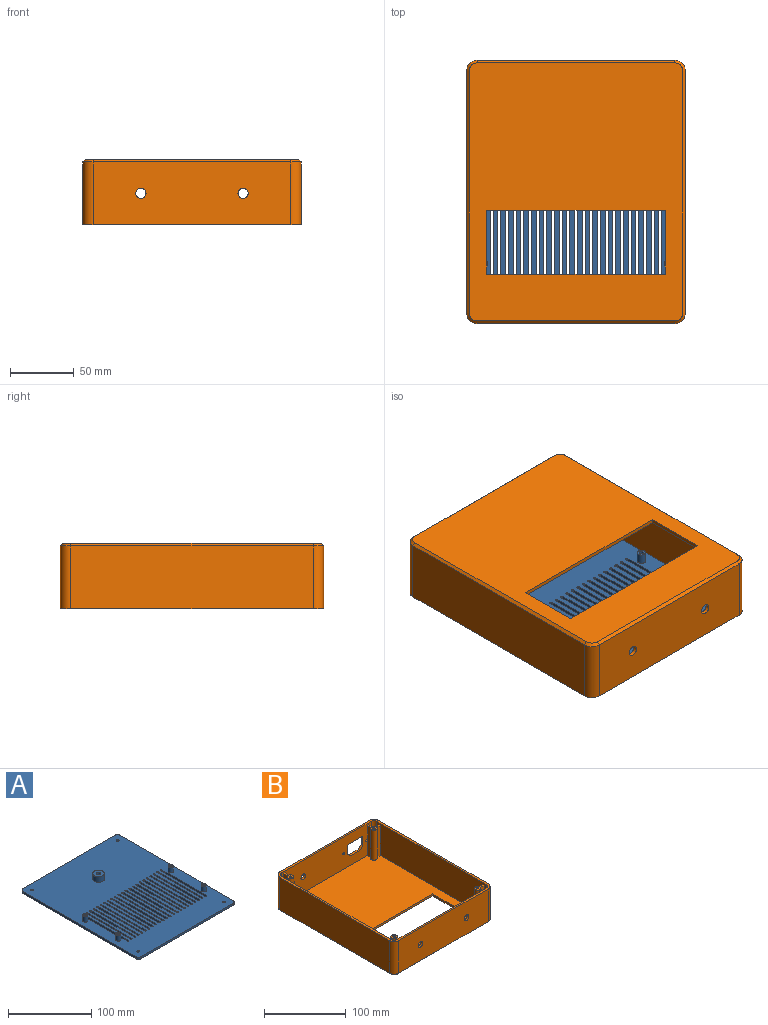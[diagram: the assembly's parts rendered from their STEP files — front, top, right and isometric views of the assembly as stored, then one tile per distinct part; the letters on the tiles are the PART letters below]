
ASSEMBLY  parts=2 mates=1
PART A: 126 faces, bbox 165x200x11 mm
  f0: plane 200x165mm, normal (0,0,1), area 28777.3mm2, adj f2,f3,f4,f5,f6,f9,f12,f15
  f1: plane 200x165mm, normal (0,0,-1), area 29063.9mm2, adj f2,f3,f4,f5,f21,f22,f23,f24
  f2: plane 155x3mm, normal (0,-1,0), area 465mm2, adj f0,f1,f21,f24
  f3: plane 190x3mm, normal (1,0,0), area 570mm2, adj f0,f1,f21,f22
  f4: plane 155x3mm, normal (0,1,0), area 465mm2, adj f0,f1,f22,f23
  f5: plane 190x3mm, normal (-1,0,0), area 570mm2, adj f0,f1,f23,f24
  f6: cylinder r=3.25mm len=8mm, axis (0,0,-1), area 163.4mm2, adj f0,f7
  f7: plane 6.5x6.5mm, normal (0,0,1), area 25.6mm2, adj f6,f28
  f8: plane 2.9x2.9mm, normal (0,0,1), area 6.6mm2, adj f28
  f9: cylinder r=3.25mm len=8mm, axis (0,0,-1), area 163.4mm2, adj f0,f10
  f10: plane 6.5x6.5mm, normal (0,0,1), area 25.6mm2, adj f9,f29
  f11: plane 2.9x2.9mm, normal (0,0,1), area 6.6mm2, adj f29
  f12: cylinder r=3.25mm len=8mm, axis (0,0,-1), area 163.4mm2, adj f0,f13
  f13: plane 6.5x6.5mm, normal (0,0,1), area 25.6mm2, adj f12,f26
  f14: plane 2.9x2.9mm, normal (0,0,1), area 6.6mm2, adj f26
  f15: cylinder r=3.25mm len=8mm, axis (0,0,-1), area 163.4mm2, adj f0,f16
  f16: plane 6.5x6.5mm, normal (0,0,1), area 25.6mm2, adj f15,f27
  f17: plane 2.9x2.9mm, normal (0,0,1), area 6.6mm2, adj f27
  f18: cylinder r=7mm len=14mm, axis (0,0,-1), area 351.9mm2, adj f0,f19
  f19: plane 14x14mm, normal (0,0,1), area 132.7mm2, adj f18,f25
  f20: plane 4.8x4.8mm, normal (0,0,1), area 18.1mm2, adj f25
  f21: cylinder r=5mm len=5mm, axis (0,0,1), area 23.6mm2, adj f0,f1,f2,f3
  f22: cylinder r=5mm len=5mm, axis (0,0,-1), area 23.6mm2, adj f0,f1,f3,f4
  f23: cylinder r=5mm len=5mm, axis (0,0,1), area 23.6mm2, adj f0,f1,f4,f5
  f24: cylinder r=5mm len=5mm, axis (0,0,-1), area 23.6mm2, adj f0,f1,f2,f5
  f25: cone r=2.4mm half-angle=1.4deg, axis (0,0,1), area 125.7mm2, adj f19,f20
  f26: cone r=1.45mm half-angle=0.7deg, axis (0,0,1), area 75.4mm2, adj f13,f14
  f27: cone r=1.45mm half-angle=0.7deg, axis (0,0,1), area 75.4mm2, adj f16,f17
  f28: cone r=1.45mm half-angle=0.7deg, axis (0,0,1), area 75.4mm2, adj f7,f8
  f29: cone r=1.45mm half-angle=0.7deg, axis (0,0,1), area 75.4mm2, adj f10,f11
  f30: cylinder r=1.1mm len=3mm, axis (0,0,1), area 10.4mm2, adj f0,f1,f31,f32
  f31: plane 75x3mm, normal (-1,0,0), area 225mm2, adj f0,f1,f30,f33
  f32: plane 75x3mm, normal (1,0,0), area 225mm2, adj f0,f1,f30,f33
  f33: cylinder r=1.1mm len=3mm, axis (0,0,1), area 10.4mm2, adj f0,f1,f31,f32
  f34: plane 75x3mm, normal (1,0,0), area 225mm2, adj f0,f1,f35,f36
  f35: cylinder r=1.1mm len=3mm, axis (0,0,1), area 10.4mm2, adj f0,f1,f34,f37
  f36: cylinder r=1.1mm len=3mm, axis (0,0,1), area 10.4mm2, adj f0,f1,f34,f37
  f37: plane 75x3mm, normal (-1,0,0), area 225mm2, adj f0,f1,f35,f36
  f38: plane 75x3mm, normal (-1,0,0), area 225mm2, adj f0,f1,f39,f41
  f39: cylinder r=1.1mm len=3mm, axis (0,0,1), area 10.4mm2, adj f0,f1,f38,f40
  f40: plane 75x3mm, normal (1,0,0), area 225mm2, adj f0,f1,f39,f41
  f41: cylinder r=1.1mm len=3mm, axis (0,0,1), area 10.4mm2, adj f0,f1,f38,f40
  f42: plane 75x3mm, normal (1,0,0), area 225mm2, adj f0,f1,f43,f44
  f43: cylinder r=1.1mm len=3mm, axis (0,0,1), area 10.4mm2, adj f0,f1,f42,f45
  f44: cylinder r=1.1mm len=3mm, axis (0,0,1), area 10.4mm2, adj f0,f1,f42,f45
  f45: plane 75x3mm, normal (-1,0,0), area 225mm2, adj f0,f1,f43,f44
  f46: plane 75x3mm, normal (-1,0,0), area 225mm2, adj f0,f1,f47,f49
  f47: cylinder r=1.1mm len=3mm, axis (0,0,1), area 10.4mm2, adj f0,f1,f46,f48
  f48: plane 75x3mm, normal (1,0,0), area 225mm2, adj f0,f1,f47,f49
  f49: cylinder r=1.1mm len=3mm, axis (0,0,1), area 10.4mm2, adj f0,f1,f46,f48
  f50: plane 75x3mm, normal (-1,0,0), area 225mm2, adj f0,f1,f51,f53
  f51: cylinder r=1.1mm len=3mm, axis (0,0,1), area 10.4mm2, adj f0,f1,f50,f52
  f52: plane 75x3mm, normal (1,0,0), area 225mm2, adj f0,f1,f51,f53
  f53: cylinder r=1.1mm len=3mm, axis (0,0,1), area 10.4mm2, adj f0,f1,f50,f52
  f54: plane 75x3mm, normal (-1,0,0), area 225mm2, adj f0,f1,f55,f57
  f55: cylinder r=1.1mm len=3mm, axis (0,0,1), area 10.4mm2, adj f0,f1,f54,f56
  f56: plane 75x3mm, normal (1,0,0), area 225mm2, adj f0,f1,f55,f57
  f57: cylinder r=1.1mm len=3mm, axis (0,0,1), area 10.4mm2, adj f0,f1,f54,f56
  f58: cylinder r=1.1mm len=3mm, axis (0,0,1), area 10.4mm2, adj f0,f1,f59,f61
  f59: plane 75x3mm, normal (-1,0,0), area 225mm2, adj f0,f1,f58,f60
  f60: cylinder r=1.1mm len=3mm, axis (0,0,1), area 10.4mm2, adj f0,f1,f59,f61
  f61: plane 75x3mm, normal (1,0,0), area 225mm2, adj f0,f1,f58,f60
  f62: cylinder r=1.1mm len=3mm, axis (0,0,1), area 10.4mm2, adj f0,f1,f63,f65
  f63: plane 75x3mm, normal (-1,0,0), area 225mm2, adj f0,f1,f62,f64
  f64: cylinder r=1.1mm len=3mm, axis (0,0,1), area 10.4mm2, adj f0,f1,f63,f65
  f65: plane 75x3mm, normal (1,0,0), area 225mm2, adj f0,f1,f62,f64
  f66: cylinder r=1.1mm len=3mm, axis (0,0,1), area 10.4mm2, adj f0,f1,f67,f69
  f67: plane 75x3mm, normal (-1,0,0), area 225mm2, adj f0,f1,f66,f68
  f68: cylinder r=1.1mm len=3mm, axis (0,0,1), area 10.4mm2, adj f0,f1,f67,f69
  f69: plane 75x3mm, normal (1,0,0), area 225mm2, adj f0,f1,f66,f68
  f70: cylinder r=1.1mm len=3mm, axis (0,0,1), area 10.4mm2, adj f0,f1,f71,f73
  f71: plane 75x3mm, normal (-1,0,0), area 225mm2, adj f0,f1,f70,f72
  f72: cylinder r=1.1mm len=3mm, axis (0,0,1), area 10.4mm2, adj f0,f1,f71,f73
  f73: plane 75x3mm, normal (1,0,0), area 225mm2, adj f0,f1,f70,f72
  f74: cylinder r=1.1mm len=3mm, axis (0,0,1), area 10.4mm2, adj f0,f1,f75,f77
  f75: plane 75x3mm, normal (-1,0,0), area 225mm2, adj f0,f1,f74,f76
  f76: cylinder r=1.1mm len=3mm, axis (0,0,1), area 10.4mm2, adj f0,f1,f75,f77
  f77: plane 75x3mm, normal (1,0,0), area 225mm2, adj f0,f1,f74,f76
  f78: cylinder r=1.1mm len=3mm, axis (0,0,1), area 10.4mm2, adj f0,f1,f79,f81
  f79: plane 75x3mm, normal (-1,0,0), area 225mm2, adj f0,f1,f78,f80
  f80: cylinder r=1.1mm len=3mm, axis (0,0,1), area 10.4mm2, adj f0,f1,f79,f81
  f81: plane 75x3mm, normal (1,0,0), area 225mm2, adj f0,f1,f78,f80
  f82: cylinder r=1.1mm len=3mm, axis (0,0,1), area 10.4mm2, adj f0,f1,f83,f85
  f83: plane 75x3mm, normal (-1,0,0), area 225mm2, adj f0,f1,f82,f84
  f84: cylinder r=1.1mm len=3mm, axis (0,0,1), area 10.4mm2, adj f0,f1,f83,f85
  f85: plane 75x3mm, normal (1,0,0), area 225mm2, adj f0,f1,f82,f84
  f86: cylinder r=1.1mm len=3mm, axis (0,0,1), area 10.4mm2, adj f0,f1,f87,f89
  f87: plane 75x3mm, normal (-1,0,0), area 225mm2, adj f0,f1,f86,f88
  f88: cylinder r=1.1mm len=3mm, axis (0,0,1), area 10.4mm2, adj f0,f1,f87,f89
  f89: plane 75x3mm, normal (1,0,0), area 225mm2, adj f0,f1,f86,f88
  f90: plane 75x3mm, normal (-1,0,0), area 225mm2, adj f0,f1,f91,f93
  f91: cylinder r=1.1mm len=3mm, axis (0,0,1), area 10.4mm2, adj f0,f1,f90,f92
  f92: plane 75x3mm, normal (1,0,0), area 225mm2, adj f0,f1,f91,f93
  f93: cylinder r=1.1mm len=3mm, axis (0,0,1), area 10.4mm2, adj f0,f1,f90,f92
  f94: cylinder r=1.1mm len=3mm, axis (0,0,1), area 10.4mm2, adj f0,f1,f95,f97
  f95: plane 75x3mm, normal (-1,0,0), area 225mm2, adj f0,f1,f94,f96
  f96: cylinder r=1.1mm len=3mm, axis (0,0,1), area 10.4mm2, adj f0,f1,f95,f97
  f97: plane 75x3mm, normal (1,0,0), area 225mm2, adj f0,f1,f94,f96
  f98: cylinder r=1.1mm len=3mm, axis (0,0,1), area 10.4mm2, adj f0,f1,f99,f101
  f99: plane 75x3mm, normal (-1,0,0), area 225mm2, adj f0,f1,f98,f100
  f100: cylinder r=1.1mm len=3mm, axis (0,0,1), area 10.4mm2, adj f0,f1,f99,f101
  f101: plane 75x3mm, normal (1,0,0), area 225mm2, adj f0,f1,f98,f100
  f102: cylinder r=1.1mm len=3mm, axis (0,0,1), area 10.4mm2, adj f0,f1,f103,f105
  f103: plane 75x3mm, normal (-1,0,0), area 225mm2, adj f0,f1,f102,f104
  f104: cylinder r=1.1mm len=3mm, axis (0,0,1), area 10.4mm2, adj f0,f1,f103,f105
  f105: plane 75x3mm, normal (1,0,0), area 225mm2, adj f0,f1,f102,f104
  f106: plane 75x3mm, normal (-1,0,0), area 225mm2, adj f0,f1,f107,f109
  f107: cylinder r=1.1mm len=3mm, axis (0,0,1), area 10.4mm2, adj f0,f1,f106,f108
  f108: plane 75x3mm, normal (1,0,0), area 225mm2, adj f0,f1,f107,f109
  f109: cylinder r=1.1mm len=3mm, axis (0,0,1), area 10.4mm2, adj f0,f1,f106,f108
  f110: plane 75x3mm, normal (-1,0,0), area 225mm2, adj f0,f1,f111,f113
  f111: cylinder r=1.1mm len=3mm, axis (0,0,1), area 10.4mm2, adj f0,f1,f110,f112
  f112: plane 75x3mm, normal (1,0,0), area 225mm2, adj f0,f1,f111,f113
  f113: cylinder r=1.1mm len=3mm, axis (0,0,1), area 10.4mm2, adj f0,f1,f110,f112
  f114: plane 75x3mm, normal (-1,0,0), area 225mm2, adj f0,f1,f115,f117
  f115: cylinder r=1.1mm len=3mm, axis (0,0,1), area 10.4mm2, adj f0,f1,f114,f116
  f116: plane 75x3mm, normal (1,0,0), area 225mm2, adj f0,f1,f115,f117
  f117: cylinder r=1.1mm len=3mm, axis (0,0,1), area 10.4mm2, adj f0,f1,f114,f116
  f118: plane 75x3mm, normal (1,0,0), area 225mm2, adj f0,f1,f119,f120
  f119: cylinder r=1.1mm len=3mm, axis (0,0,1), area 10.4mm2, adj f0,f1,f118,f121
  f120: cylinder r=1.1mm len=3mm, axis (0,0,1), area 10.4mm2, adj f0,f1,f118,f121
  f121: plane 75x3mm, normal (-1,0,0), area 225mm2, adj f0,f1,f119,f120
  f122: cylinder r=1.6mm len=3.2mm, axis (0,0,1), area 30.2mm2, adj f0,f1
  f123: cylinder r=1.6mm len=3.2mm, axis (0,0,1), area 30.2mm2, adj f0,f1
  f124: cylinder r=1.6mm len=3.2mm, axis (0,0,1), area 30.2mm2, adj f0,f1
  f125: cylinder r=1.6mm len=3.2mm, axis (0,0,1), area 30.2mm2, adj f0,f1
PART B: 84 faces, bbox 171x206x51 mm
  f0: plane 8.9x8.9mm, normal (0,0,1), area 68.8mm2, adj f2,f3,f8,f26,f76,f82
  f1: plane 200x165mm, normal (0,0,1), area 25396mm2, adj f2,f6,f7,f8,f10,f14,f33,f37
  f2: plane 155x48mm, normal (0,-1,0), area 6643.1mm2, adj f0,f1,f4,f15,f25,f26,f36,f40
  f3: cylinder r=4mm len=45mm, axis (0,0,-1), area 182.5mm2, adj f0,f36,f76,f82
  f4: plane 8.9x8.9mm, normal (0,0,1), area 68.8mm2, adj f2,f5,f6,f25,f77,f81
  f5: cylinder r=4mm len=45mm, axis (0,0,-1), area 182.5mm2, adj f4,f40,f77,f81
  f6: plane 190x48mm, normal (-1,0,0), area 8922mm2, adj f1,f4,f9,f15,f25,f28,f32,f40
  f7: cylinder r=4mm len=45mm, axis (0,0,-1), area 747.9mm2, adj f1,f40,f78,f80
  f8: plane 190x48mm, normal (1,0,0), area 8922mm2, adj f0,f1,f13,f15,f26,f27,f29,f36
  f9: plane 8.9x8.9mm, normal (0,0,1), area 68.8mm2, adj f6,f10,f11,f28,f72,f74
  f10: plane 155x48mm, normal (0,1,0), area 7141.5mm2, adj f1,f9,f13,f15,f27,f28,f29,f32
  f11: cylinder r=4mm len=45mm, axis (0,0,-1), area 182.5mm2, adj f9,f32,f72,f74
  f12: cylinder r=4mm len=45mm, axis (0,0,-1), area 182.5mm2, adj f13,f29,f67,f69
  f13: plane 8.9x8.9mm, normal (0,0,1), area 68.8mm2, adj f8,f10,f12,f27,f67,f69
  f14: cylinder r=4mm len=45mm, axis (0,0,-1), area 747.9mm2, adj f1,f29,f68,f70
  f15: plane 206x171mm, normal (0,0,1), area 2192.5mm2, adj f2,f6,f8,f10,f16,f17,f18,f19
  f16: plane 190x49mm, normal (1,0,0), area 9310mm2, adj f15,f21,f24,f43
  f17: plane 155x49mm, normal (0,1,0), area 6996mm2, adj f15,f21,f22,f46,f53,f54,f55,f56
  f18: plane 190x49mm, normal (-1,0,0), area 9310mm2, adj f15,f22,f23,f50
  f19: plane 155x49mm, normal (0,-1,0), area 7494.5mm2, adj f15,f23,f24,f47,f51,f52
  f20: plane 202x167mm, normal (0,0,-1), area 26703.1mm2, adj f43,f44,f45,f46,f47,f48,f49,f50
  f21: cylinder r=8mm len=49mm, axis (0,0,1), area 615.8mm2, adj f15,f16,f17,f44
  f22: cylinder r=8mm len=49mm, axis (0,0,-1), area 615.8mm2, adj f15,f17,f18,f48
  f23: cylinder r=8mm len=49mm, axis (0,0,1), area 615.8mm2, adj f15,f18,f19,f49
  f24: cylinder r=8mm len=49mm, axis (0,0,-1), area 615.8mm2, adj f15,f16,f19,f45
  f25: cylinder r=5mm len=48mm, axis (0,0,1), area 377mm2, adj f2,f4,f6,f15
  f26: cylinder r=5mm len=48mm, axis (0,0,-1), area 377mm2, adj f0,f2,f8,f15
  f27: cylinder r=5mm len=48mm, axis (0,0,1), area 377mm2, adj f8,f10,f13,f15
  f28: cylinder r=5mm len=48mm, axis (0,0,-1), area 377mm2, adj f6,f9,f10,f15
  f29: plane 14x14mm, normal (0,0,1), area 70.3mm2, adj f8,f10,f12,f14,f30,f67,f68,f69
  f30: cylinder r=1.45mm len=45mm, axis (0,0,-1), area 410mm2, adj f29,f31
  f31: plane 2.9x2.9mm, normal (0,0,1), area 6.6mm2, adj f30
  f32: plane 14x14mm, normal (0,0,1), area 70.3mm2, adj f6,f10,f11,f33,f34,f71,f72,f73
  f33: cylinder r=4mm len=45mm, axis (0,0,-1), area 747.9mm2, adj f1,f32,f71,f73
  f34: cylinder r=1.45mm len=45mm, axis (0,0,-1), area 410mm2, adj f32,f35
  f35: plane 2.9x2.9mm, normal (0,0,1), area 6.6mm2, adj f34
  f36: plane 14x14mm, normal (0,0,1), area 70.3mm2, adj f2,f3,f8,f37,f38,f75,f76,f82
  f37: cylinder r=4mm len=45mm, axis (0,0,-1), area 747.9mm2, adj f1,f36,f75,f83
  f38: cylinder r=1.45mm len=45mm, axis (0,0,-1), area 410mm2, adj f36,f39
  f39: plane 2.9x2.9mm, normal (0,0,1), area 6.6mm2, adj f38
  f40: plane 14x14mm, normal (0,0,1), area 70.3mm2, adj f2,f5,f6,f7,f41,f77,f78,f80
  f41: cylinder r=1.45mm len=45mm, axis (0,0,-1), area 410mm2, adj f40,f42
  f42: plane 2.9x2.9mm, normal (0,0,1), area 6.6mm2, adj f41
  f43: plane 190x2mm, normal (0.71,0,-0.71), area 537.4mm2, adj f16,f20,f44,f45
  f44: cone r=6mm half-angle=45deg, axis (0,0,1), area 31.1mm2, adj f20,f21,f43,f46
  f45: cone r=6mm half-angle=45deg, axis (0,0,1), area 31.1mm2, adj f20,f24,f43,f47
  f46: plane 155x2mm, normal (0,0.71,-0.71), area 438.4mm2, adj f17,f20,f44,f48
  f47: plane 155x2mm, normal (0,-0.71,-0.71), area 438.4mm2, adj f19,f20,f45,f49
  f48: cone r=6mm half-angle=45deg, axis (0,0,1), area 31.1mm2, adj f20,f22,f46,f50
  f49: cone r=6mm half-angle=45deg, axis (0,0,1), area 31.1mm2, adj f20,f23,f47,f50
  f50: plane 190x2mm, normal (-0.71,0,-0.71), area 537.4mm2, adj f18,f20,f48,f49
  f51: cylinder r=4mm len=8mm, axis (0,-1,0), area 75.4mm2, adj f10,f19
  f52: cylinder r=4mm len=8mm, axis (0,-1,0), area 75.4mm2, adj f10,f19
  f53: cylinder r=4mm len=8mm, axis (0,1,0), area 75.4mm2, adj f2,f17
  f54: plane 13.61x3mm, normal (-1,0,0), area 40.8mm2, adj f2,f17,f55,f57
  f55: plane 5.5x5.39mm, normal (-0.7,0,0.71), area 23.1mm2, adj f2,f17,f54,f56
  f56: plane 16x3mm, normal (0,0,1), area 48mm2, adj f2,f17,f55,f58
  f57: plane 27x3mm, normal (0,0,-1), area 81mm2, adj f2,f17,f54,f59
  f58: plane 5.5x5.39mm, normal (0.7,0,0.71), area 23.1mm2, adj f2,f17,f56,f59
  f59: plane 13.61x3mm, normal (1,0,0), area 40.8mm2, adj f2,f17,f57,f58
  f60: cylinder r=1.55mm len=3.1mm, axis (0,1,0), area 29.2mm2, adj f2,f17
  f61: cylinder r=1.55mm len=3.1mm, axis (0,1,0), area 29.2mm2, adj f2,f17,f79
  f62: cylinder r=4mm len=8mm, axis (0,1,0), area 75.4mm2, adj f2,f17
  f63: plane 50x3mm, normal (-1,0,0), area 150mm2, adj f1,f20,f64,f65
  f64: plane 140x3mm, normal (0,1,0), area 420mm2, adj f1,f20,f63,f66
  f65: plane 140x3mm, normal (0,-1,0), area 420mm2, adj f1,f20,f63,f66
  f66: plane 50x3mm, normal (1,0,0), area 150mm2, adj f1,f20,f64,f65
  f67: plane 45x6.15mm, normal (0,-1,0), area 276.9mm2, adj f8,f12,f13,f29
  f68: plane 45x6.15mm, normal (0,1,0), area 276.9mm2, adj f1,f8,f14,f29
  f69: plane 45x6.15mm, normal (-1,0,0), area 276.9mm2, adj f10,f12,f13,f29
  f70: plane 45x6.15mm, normal (1,0,0), area 276.9mm2, adj f1,f10,f14,f29
  f71: plane 45x6.15mm, normal (0,1,0), area 276.9mm2, adj f1,f6,f32,f33
  f72: plane 45x6.15mm, normal (0,-1,0), area 276.9mm2, adj f6,f9,f11,f32
  f73: plane 45x6.15mm, normal (-1,0,0), area 276.9mm2, adj f1,f10,f32,f33
  f74: plane 45x6.15mm, normal (1,0,0), area 276.9mm2, adj f9,f10,f11,f32
  f75: plane 45x6.15mm, normal (0,-1,0), area 276.9mm2, adj f1,f8,f36,f37
  f76: plane 45x6.15mm, normal (0,1,0), area 276.9mm2, adj f0,f3,f8,f36
  f77: plane 45x6.15mm, normal (0,1,0), area 276.9mm2, adj f4,f5,f6,f40
  f78: plane 45x6.15mm, normal (0,-1,0), area 276.9mm2, adj f1,f6,f7,f40
  f79: plane 1.33x0.15mm, normal (0,1,0), area 0.1mm2, adj f61,f80
  f80: plane 45x6.15mm, normal (-1,0,0), area 276.9mm2, adj f1,f2,f7,f40,f79
  f81: plane 45x6.15mm, normal (1,0,0), area 276.9mm2, adj f2,f4,f5,f40
  f82: plane 45x6.15mm, normal (-1,0,0), area 276.9mm2, adj f0,f2,f3,f36
  f83: plane 45x6.15mm, normal (1,0,0), area 276.9mm2, adj f1,f2,f36,f37
PLACE A t=(0,-3.73,0)mm
PLACE B rot(axis=(0,1,0),180deg) t=(0,-3.73,51)mm
MATE fastened A.f123 <-> B.f12  axis (0,0,1) through (72.5,-93.73,3)mm
